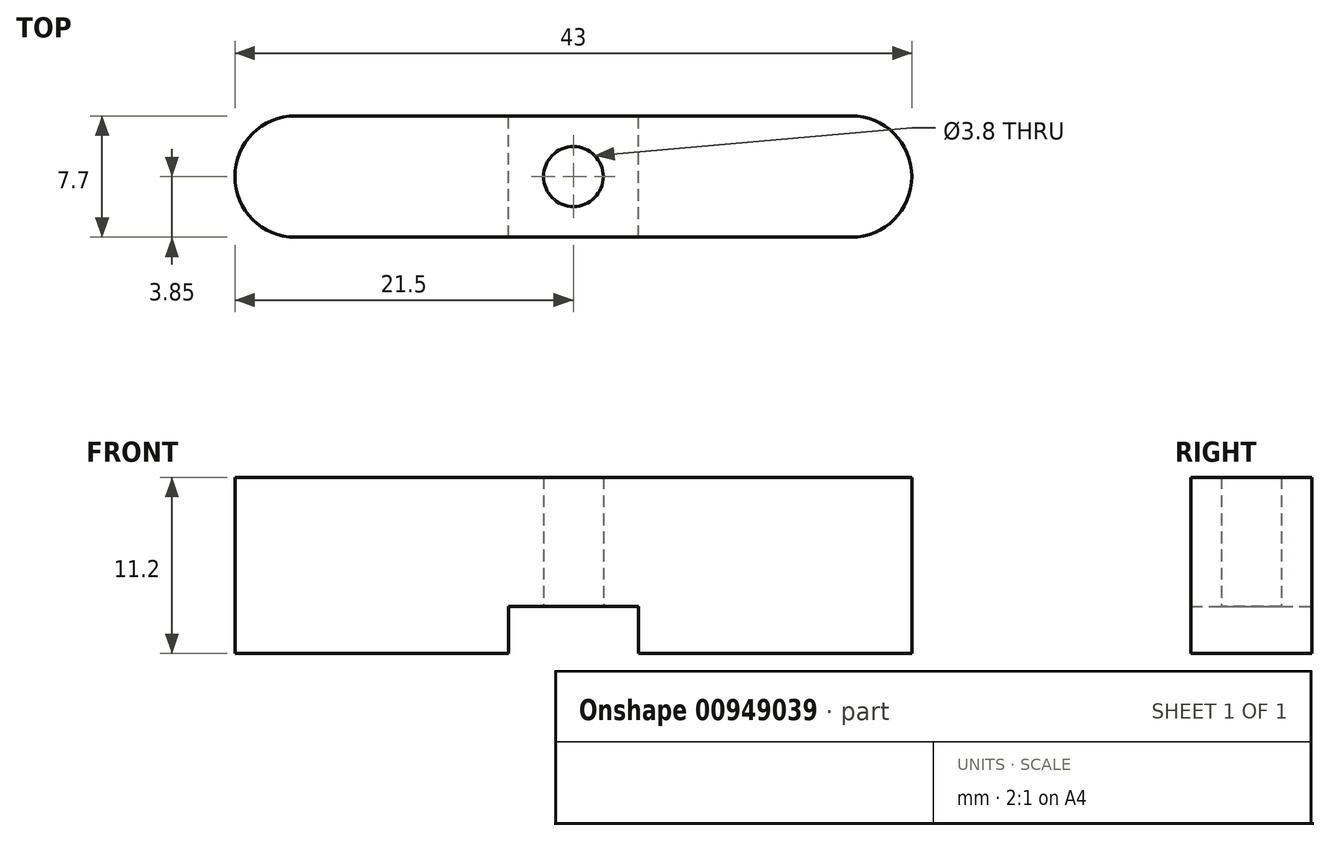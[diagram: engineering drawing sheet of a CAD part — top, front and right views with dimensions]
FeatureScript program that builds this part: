
annotation { "Feature Type Name" : "Feature", "Feature Type Description" : "" }
export const myFeature = defineFeature(function(context is Context, id is Id, definition is map)
    precondition{}
    {
        {
            var Q0;
            Q0=qCreatedBy(makeId("Top.planeOp"),FACE);
            var sketch = newSketch(context, id + "F0", { "sketchPlane" : qUnion([Q0])});
            skLineSegment(sketch, "E0.bottom", {"start": v(21.5, 3.85) * mm, "end": v(-21.5, 3.85) * mm});
            skLineSegment(sketch, "E0.top", {"start": v(21.5, -3.85) * mm, "end": v(-21.5, -3.85) * mm});
            skLineSegment(sketch, "E0.left", {"start": v(21.5, 3.85) * mm, "end": v(21.5, -3.85) * mm});
            skLineSegment(sketch, "E0.right", {"start": v(-21.5, 3.85) * mm, "end": v(-21.5, -3.85) * mm});
            skPoint(sketch, "E0.middle", {"position": v(0, 0) * mm});
            skSolve(sketch);
        }
        {
            var Q0;
            Q0=makeQuery(id+"F0.imprint","IMPRINT",FACE,{"disambiguationData":[TD([[makeQuery(id+"F0.imprint","IMPRINT",EDGE,{"derivedFrom":sQuery(id+"F0.wireOp",EDGE,"E0.bottom")}),1.0]])]});
            var sketch = newSketch(context, id + "F1", { "sketchPlane" : qUnion([Q0])});
            skCircle(sketch, "E1", {"center": v(0, 0) * mm, "radius": 1.9 * mm});
            skSolve(sketch);
        }
        {
            var Q0;
            Q0=makeQuery(id+"F1.imprint","IMPRINT",FACE,{"disambiguationData":[TD([[makeQuery(id+"F1.imprint","IMPRINT",EDGE,{"derivedFrom":sQuery(id+"F1.wireOp",EDGE,"E1")}),-1.0]])]});
            var sketch = newSketch(context, id + "F2", { "sketchPlane" : qUnion([Q0])});
            skCircle(sketch, "E2", {"center": v(0, 0) * mm, "radius": 3.4 * mm});
            skSolve(sketch);
        }
        {
            var Q0;
            Q0=makeQuery(id+"F1.imprint","IMPRINT",FACE,{"disambiguationData":[TD([[makeQuery(id+"F1.imprint","IMPRINT",EDGE,{"derivedFrom":sQuery(id+"F1.wireOp",EDGE,"E1")}),-1.0]])]});
            extrude(context, id + "F3", {"entities" : qUnion([Q0]), "depth" : 11.2 * mm, "offsetDistance" : 25 * mm});
        }
        {
            var Q0;
            Q0=makeQuery(id+"F2.imprint","IMPRINT",FACE,{"disambiguationData":[TD([[makeQuery(id+"F2.imprint","IMPRINT",EDGE,{"derivedFrom":sQuery(id+"F2.wireOp",EDGE,"E2")}),1.0]])]});
            var Q1;
            Q1=sQuery(id+"F2.wireOp",EDGE,"E2");
            extrude(context, id + "F4", {"entities" : qUnion([Q0]), "operationType" : NewBodyOperationType.REMOVE, "surfaceEntities" : qUnion([Q1]), "depth" : 3 * mm, "offsetDistance" : 25 * mm});
        }
        {
            var Q0;
            Q0=makeQuery(id+"F3.opExtrude","SWEPT_EDGE",EDGE,{"disambiguationData":[OSD([sQuery(id+"F0.wireOp",EDGE,"E0.top"),sQuery(id+"F0.wireOp",EDGE,"E0.right")])]});
            var Q1;
            Q1=makeQuery(id+"F3.opExtrude","SWEPT_EDGE",EDGE,{"disambiguationData":[OSD([sQuery(id+"F0.wireOp",EDGE,"E0.bottom"),sQuery(id+"F0.wireOp",EDGE,"E0.right")])]});
            var Q2;
            Q2=makeQuery(id+"F3.opExtrude","SWEPT_EDGE",EDGE,{"disambiguationData":[OSD([sQuery(id+"F0.wireOp",EDGE,"E0.top"),sQuery(id+"F0.wireOp",EDGE,"E0.left")])]});
            var Q3;
            Q3=makeQuery(id+"F3.opExtrude","SWEPT_EDGE",EDGE,{"disambiguationData":[OSD([sQuery(id+"F0.wireOp",EDGE,"E0.bottom"),sQuery(id+"F0.wireOp",EDGE,"E0.left")])]});
            fillet(context, id + "F5", {"entities" : qUnion([Q0, Q1, Q2, Q3]), "radius" : 3.85 * mm, "tangentPropagation" : true, "allowEdgeOverflow" : false});
        }
        {
            var Q0;
            Q0=makeQuery(id+"F0.imprint","IMPRINT",FACE,{"disambiguationData":[TD([[makeQuery(id+"F0.imprint","IMPRINT",EDGE,{"derivedFrom":sQuery(id+"F0.wireOp",EDGE,"E0.bottom")}),1.0]])]});
            var sketch = newSketch(context, id + "F6", { "sketchPlane" : qUnion([Q0])});
            skLineSegment(sketch, "E3.bottom", {"start": v(4.13, -10.97) * mm, "end": v(-4.13, -10.97) * mm});
            skLineSegment(sketch, "E3.top", {"start": v(4.13, 10.97) * mm, "end": v(-4.13, 10.97) * mm});
            skLineSegment(sketch, "E3.left", {"start": v(4.13, -10.97) * mm, "end": v(4.13, 10.97) * mm});
            skLineSegment(sketch, "E3.right", {"start": v(-4.13, -10.97) * mm, "end": v(-4.13, 10.97) * mm});
            skPoint(sketch, "E3.middle", {"position": v(0, 0) * mm});
            skSolve(sketch);
        }
        {
            var Q0;
            {var subQ0=sQuery(id+"F6.wireOp",EDGE,"E3.left");var subQ1=makeQuery(id+"F0.imprint","IMPRINT",EDGE,{"derivedFrom":sQuery(id+"F0.wireOp",EDGE,"E0.top")});var subQ2=makeQuery(id+"F6.imprint","INTERSECT",VERTEX,{"derivedFrom":[subQ1,subQ0]});Q0=makeQuery(id+"F6.imprint","IMPRINT",FACE,{"disambiguationData":[TD([[makeQuery(id+"F6.imprint","IMPRINT",EDGE,{"disambiguationData":[TD([[subQ2,-1.0]])],"derivedFrom":subQ0}),1.0]])]});}
            var Q1;
            {var subQ0=sQuery(id+"F6.wireOp",EDGE,"E3.bottom");Q1=makeQuery(id+"F6.imprint","IMPRINT",FACE,{"disambiguationData":[TD([[makeQuery(id+"F6.imprint","IMPRINT",EDGE,{"derivedFrom":subQ0}),-1.0]])]});}
            var Q2;
            {var subQ0=sQuery(id+"F6.wireOp",EDGE,"E3.top");Q2=makeQuery(id+"F6.imprint","IMPRINT",FACE,{"disambiguationData":[TD([[makeQuery(id+"F6.imprint","IMPRINT",EDGE,{"derivedFrom":subQ0}),1.0]])]});}
            extrude(context, id + "F7", {"entities" : qUnion([Q0, Q1, Q2]), "operationType" : NewBodyOperationType.REMOVE, "depth" : 3 * mm, "offsetDistance" : 25 * mm});
        }
    });
